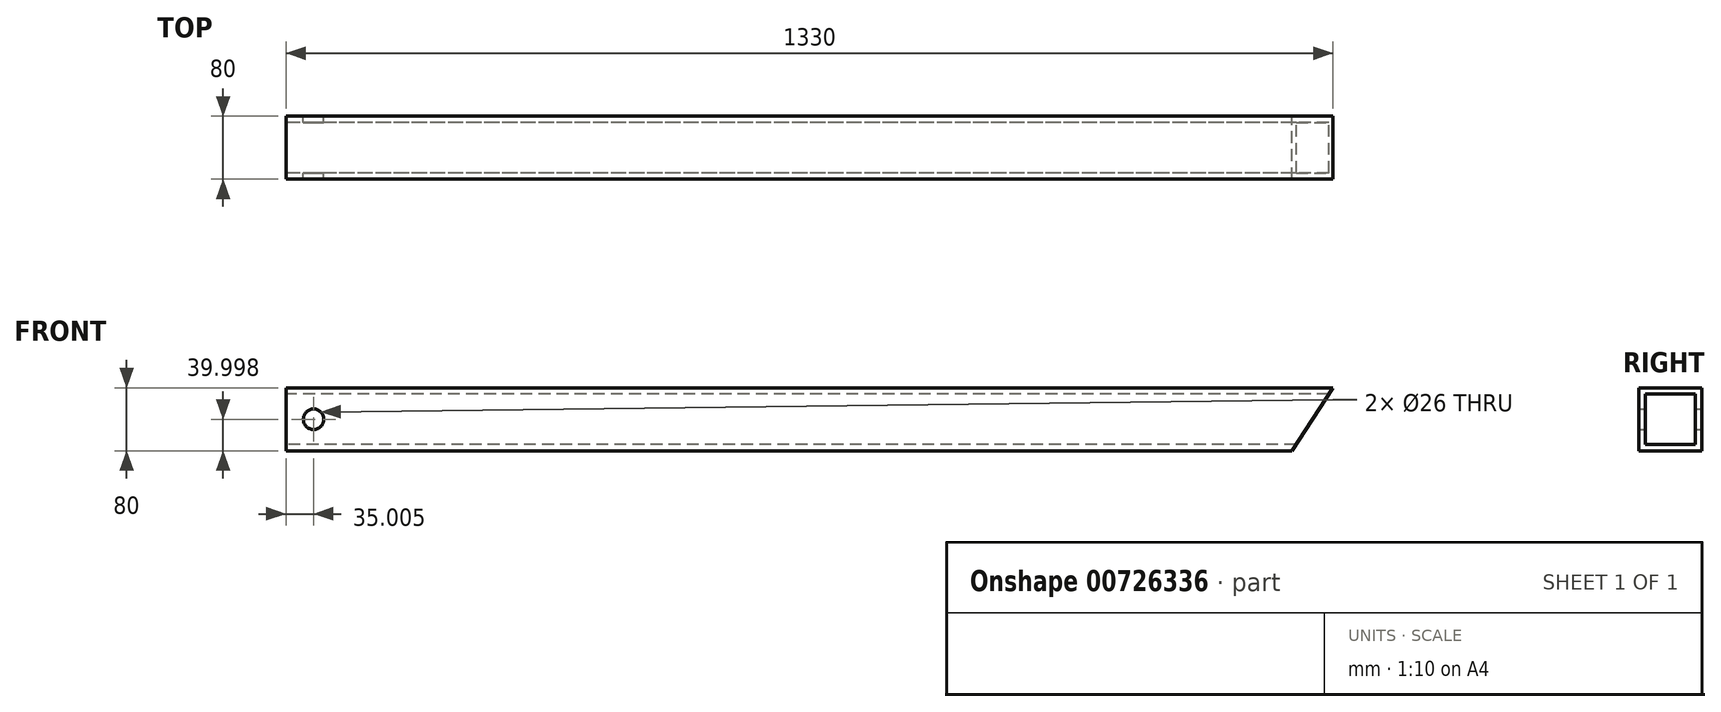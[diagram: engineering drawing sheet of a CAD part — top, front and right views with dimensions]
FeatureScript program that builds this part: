
annotation { "Feature Type Name" : "Feature", "Feature Type Description" : "" }
export const myFeature = defineFeature(function(context is Context, id is Id, definition is map)
    precondition{}
    {
        {
            var Q0;
            Q0=qCreatedBy(makeId("Front.planeOp"),FACE);
            var sketch = newSketch(context, id + "F0", { "sketchPlane" : qUnion([Q0])});
            skLineSegment(sketch, "E0", {"start": v(-687.84, 48.15) * mm, "end": v(642.16, 48.15) * mm});
            skLineSegment(sketch, "E1", {"start": v(642.16, 48.15) * mm, "end": v(590.21, -31.85) * mm});
            skLineSegment(sketch, "E2", {"start": v(590.21, -31.85) * mm, "end": v(-687.84, -31.85) * mm});
            skLineSegment(sketch, "E3", {"start": v(-687.84, -31.85) * mm, "end": v(-687.84, 48.15) * mm});
            skPoint(sketch, "E4", {"position": v(-652.84, 8.15) * mm});
            skPoint(sketch, "E4.positionSnap0", {"position": v(-687.84, 8.15) * mm});
            skSolve(sketch);
        }
        {
            var Q0;
            Q0=makeQuery(id+"F0.imprint","IMPRINT",FACE,{"disambiguationData":[TD([[makeQuery(id+"F0.imprint","IMPRINT",EDGE,{"derivedFrom":sQuery(id+"F0.wireOp",EDGE,"E0")}),-1.0]])]});
            extrude(context, id + "F1", {"entities" : qUnion([Q0]), "depth" : 80 * mm, "offsetDistance" : 25 * mm});
        }
        {
            var Q0;
            Q0=makeQuery(id+"F1.opExtrude","SWEPT_FACE",FACE,{"disambiguationData":[OSD([sQuery(id+"F0.wireOp",EDGE,"E3")])]});
            var sketch = newSketch(context, id + "F2", { "sketchPlane" : qUnion([Q0])});
            skLineSegment(sketch, "E5.bottom", {"start": v(8, 40.15) * mm, "end": v(72, 40.15) * mm});
            skLineSegment(sketch, "E5.top", {"start": v(8, -23.85) * mm, "end": v(72, -23.85) * mm});
            skLineSegment(sketch, "E5.left", {"start": v(8, 40.15) * mm, "end": v(8, -23.85) * mm});
            skLineSegment(sketch, "E5.right", {"start": v(72, 40.15) * mm, "end": v(72, -23.85) * mm});
            skSolve(sketch);
        }
        {
            var Q0;
            Q0=makeQuery(id+"F2.imprint","IMPRINT",FACE,{"disambiguationData":[TD([[makeQuery(id+"F2.imprint","IMPRINT",EDGE,{"derivedFrom":sQuery(id+"F2.wireOp",EDGE,"E5.bottom")}),-1.0]])]});
            extrude(context, id + "F3", {"entities" : qUnion([Q0]), "operationType" : NewBodyOperationType.REMOVE, "oppositeDirection" : true, "depth" : 1330 * mm, "offsetDistance" : 25 * mm});
        }
        {
            var Q0;
            Q0=sQuery(id+"F0.wireOp",VERTEX,"E4");
            var Q1;
            Q1=makeQuery(id+"F1.opExtrude","SWEPT_BODY",BODY,{"disambiguationData":[OSD([sQuery(id+"F0.wireOp",EDGE,"E0"),sQuery(id+"F0.wireOp",EDGE,"E1"),sQuery(id+"F0.wireOp",EDGE,"E2"),sQuery(id+"F0.wireOp",EDGE,"E3")])]});
            hole(context, id + "F4", {"style" : HoleStyle.SIMPLE, "endStyle" : HoleEndStyle.THROUGH, "oppositeDirection" : true, "holeDiameter" : 26 * mm, "majorDiameter" : 5 * mm, "isTappedThrough" : true, "tappedDepth" : 12 * mm, "tapClearance" : 3, "locations" : qUnion([Q0]), "scope" : qUnion([Q1])});
        }
    });
